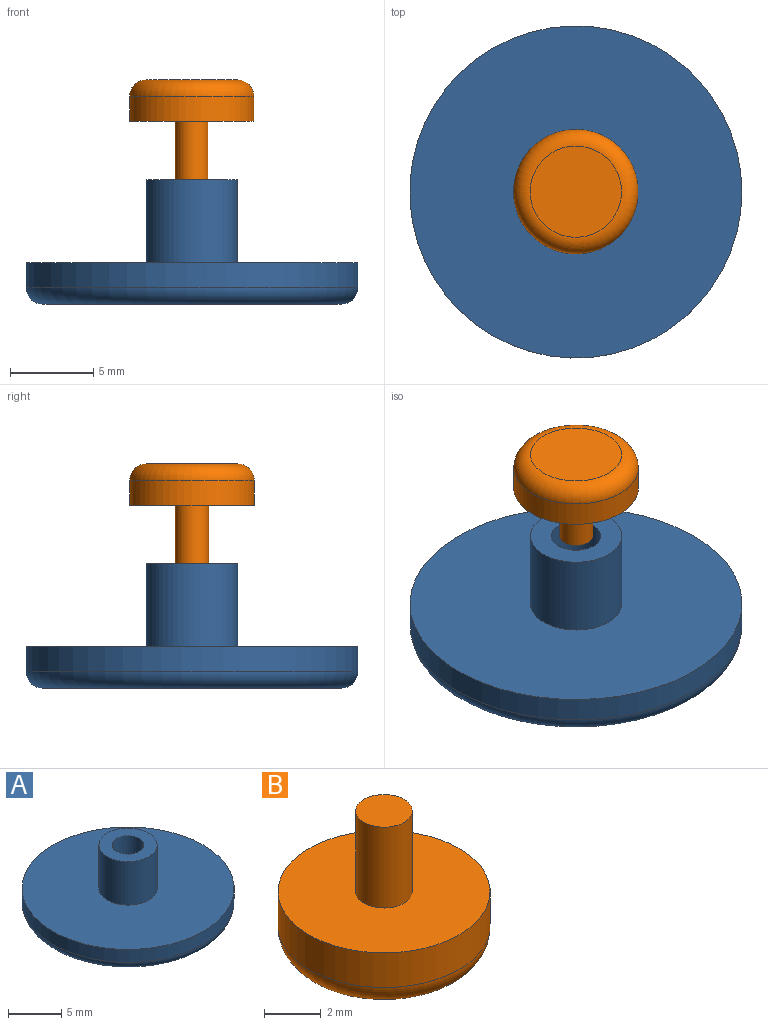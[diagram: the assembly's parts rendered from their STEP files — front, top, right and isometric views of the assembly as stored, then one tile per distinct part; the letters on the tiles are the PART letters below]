
ASSEMBLY  parts=2 mates=1
PART A: 28 faces, bbox 21.6x21.6x7.5 mm
  f0: cylinder r=10mm len=20mm, axis (0,0,-1), area 94.2mm2, adj f1,f3
  f1: plane 20x20mm, normal (0,0,1), area 290.4mm2, adj f0,f24
  f2: plane 18x18mm, normal (0,0,-1), area 35.4mm2, adj f3,f5
  f3: torus R=9mm, axis (0,0,1), area 95.1mm2, adj f0,f2
  f4: cylinder r=8.1mm len=16.2mm, axis (0,0,-1), area 25.4mm2, adj f6,f7
  f5: cylinder r=8.35mm len=16.7mm, axis (0,0,-1), area 26.2mm2, adj f2,f6
  f6: plane 16.7x16.7mm, normal (0,0,-1), area 12.9mm2, adj f4,f5
  f7: plane 16.2x16.2mm, normal (0,0,-1), area 75.4mm2, adj f4,f9
  f8: cylinder r=6.2mm len=12.4mm, axis (0,0,-1), area 19.5mm2, adj f10,f11
  f9: cylinder r=6.45mm len=12.9mm, axis (0,0,-1), area 20.3mm2, adj f7,f10
  f10: plane 12.9x12.9mm, normal (0,0,-1), area 9.9mm2, adj f8,f9
  f11: plane 12.4x12.4mm, normal (0,0,-1), area 55.7mm2, adj f8,f13
  f12: cylinder r=4.3mm len=8.6mm, axis (0,0,-1), area 13.5mm2, adj f14,f15
  f13: cylinder r=4.55mm len=9.1mm, axis (0,0,-1), area 14.3mm2, adj f11,f14
  f14: plane 9.1x9.1mm, normal (0,0,-1), area 7mm2, adj f12,f13
  f15: plane 8.6x8.6mm, normal (0,0,-1), area 36mm2, adj f12,f17
  f16: cylinder r=2.4mm len=4.8mm, axis (0,0,-1), area 7.5mm2, adj f18,f19
  f17: cylinder r=2.65mm len=5.3mm, axis (0,0,-1), area 8.3mm2, adj f15,f18
  f18: plane 5.3x5.3mm, normal (0,0,-1), area 4mm2, adj f16,f17
  f19: plane 4.8x4.8mm, normal (0,0,-1), area 16.3mm2, adj f16,f21
  f20: cylinder r=0.5mm len=1mm, axis (0,0,-1), area 1.6mm2, adj f22,f23
  f21: cylinder r=0.75mm len=1.5mm, axis (0,0,-1), area 2.4mm2, adj f19,f22
  f22: plane 1.5x1.5mm, normal (0,0,-1), area 1mm2, adj f20,f21
  f23: plane 1x1mm, normal (0,0,-1), area 0.8mm2, adj f20
  f24: cylinder r=2.75mm len=5.5mm, axis (0,0,-1), area 86.4mm2, adj f1,f25
  f25: plane 5.5x5.5mm, normal (0,0,1), area 16.7mm2, adj f24,f26
  f26: cylinder r=1.5mm len=4mm, axis (0,0,1), area 37.7mm2, adj f25,f27
  f27: plane 3x3mm, normal (0,0,1), area 7.1mm2, adj f26
PART B: 6 faces, bbox 8.1x8.1x6 mm
  f0: cylinder r=3.75mm len=7.5mm, axis (0,0,-1), area 35.3mm2, adj f1,f3
  f1: plane 7.5x7.5mm, normal (0,0,1), area 41mm2, adj f0,f4
  f2: plane 5.5x5.5mm, normal (0,0,-1), area 23.8mm2, adj f3
  f3: torus R=2.75mm, axis (0,0,1), area 33.4mm2, adj f0,f2
  f4: cylinder r=1mm len=3.5mm, axis (0,0,-1), area 22mm2, adj f1,f5
  f5: plane 2x2mm, normal (0,0,1), area 3.1mm2, adj f4
PLACE A t=(-5.27,0.24,2.22)mm
PLACE B rot(axis=(0,1,0),180deg) t=(-25.52,0.24,15.72)mm
MATE slider A.f24 <-> B.f0  axis (0,0,1) through (-5.27,0.24,9.72)mm
